# Revit family: BIMLIB_КанальныйВентилятор_SLIM_SHUFT
name_source: partatom
category: Оборудование
revit_build: Autodesk Revit 2017 (Build: 20170118_1100(x64)
units: mm (PartAtom-declared; Revit-internal decimal feet)

## family parameters
Всегда вертикально = Да
На основе рабочей плоскости = Нет
Общий = Нет
При загрузке вырезать с полостями = Нет
Размер круглого соединителя = Использовать диаметр
Тип детали = Вставляется
Точка расчета площади = Нет

## types (6) — shared parameters
ADSK_URL документации изделия = http://www.shuft.ru
ADSK_URL страницы изделия = http://www.shuft.ru
ADSK_Версия Revit = 2017
ADSK_Версия семейства = v.1
ADSK_Единица измерения = шт.
ADSK_Завод-изготовитель = ООО «Завод ВКО» марка SHUFT
ADSK_Классификация нагрузок = Прочее
ADSK_Количество фаз = 1
ADSK_Коэффициент мощности = 1
ADSK_Материал = BIMLIB_Сталь_SHUFT
ADSK_Напряжение = 230 В
ADSK_Номинальная мощность = 0 кВт
ADSK_Полная мощность = 0 кВт
BL_BIM library = https://bimlib.pro
IP Двигателя = IP44
URL = http://www.shuft.ru
Изготовитель = ООО «Завод ВКО» марка SHUFT
Климатическое исполнение = У2

## per-type parameters (varying)
| type | ADSK_Масса | ADSK_Наименование | ADSK_Размер_Высота | ADSK_Размер_Диаметр | ADSK_Размер_Длина | ADSK_Размер_Ширина | ADSK_Ток | ADSK_Частота вращения вентилятора | a | b | c | d | e | f | g | r | r1 | Глубина клеммной коробки | Ширина клеммной коробки |
| SLIM 100 | 5 | Канальный вентилятор SLIM 100 | 124 мм | 100 мм | 314 мм | 330 мм | 0 А | 2380 | 414 мм | 314 мм | 124 мм | 100 мм | 330 мм | 70 мм | 61 мм | 50 мм | 51 мм | 70 мм | 70 мм |
| SLIM 125 | 5.2 | Канальный вентилятор SLIM 125 | 150 мм | 125 мм | 314 мм | 330 мм | 0 А | 2380 | 414 мм | 314 мм | 150 мм | 125 мм | 330 мм | 83 мм | 74 мм | 63 мм | 64 мм | 70 мм | 70 мм |
| SLIM 160 | 7 | Канальный вентилятор SLIM 160 | 186 мм | 160 мм | 362 мм | 390 мм | 0 А | 2500 | 462 мм | 362 мм | 186 мм | 160 мм | 390 мм | 101 мм | 92 мм | 80 мм | 81 мм | 70 мм | 70 мм |
| SLIM 200 | 8.5 | Канальный вентилятор SLIM 200 | 226 мм | 200 мм | 372 мм | 390 мм | 1 А | 2640 | 472 мм | 372 мм | 226 мм | 200 мм | 390 мм | 121 мм | 112 мм | 100 мм | 101 мм | 70 мм | 70 мм |
| SLIM 250 | 9.7 | Канальный вентилятор SLIM 250 | 283 мм | 250 мм | 392 мм | 390 мм | 1 А | 2440 | 492 мм | 392 мм | 283 мм | 250 мм | 390 мм | 145 мм | 136 мм | 125 мм | 126 мм | 85 мм | 85 мм |
| SLIM 315 | 13.5 | Канальный вентилятор SLIM 315 | 349 мм | 315 мм | 427 мм | 444 мм | 1 А | 2500 | 527 мм | 427 мм | 349 мм | 315 мм | 444 мм | 178 мм | 169 мм | 158 мм | 159 мм | 85 мм | 85 мм |

note: column(s) folded — value = type name in every type: ADSK_Код изделия, ADSK_Марка
